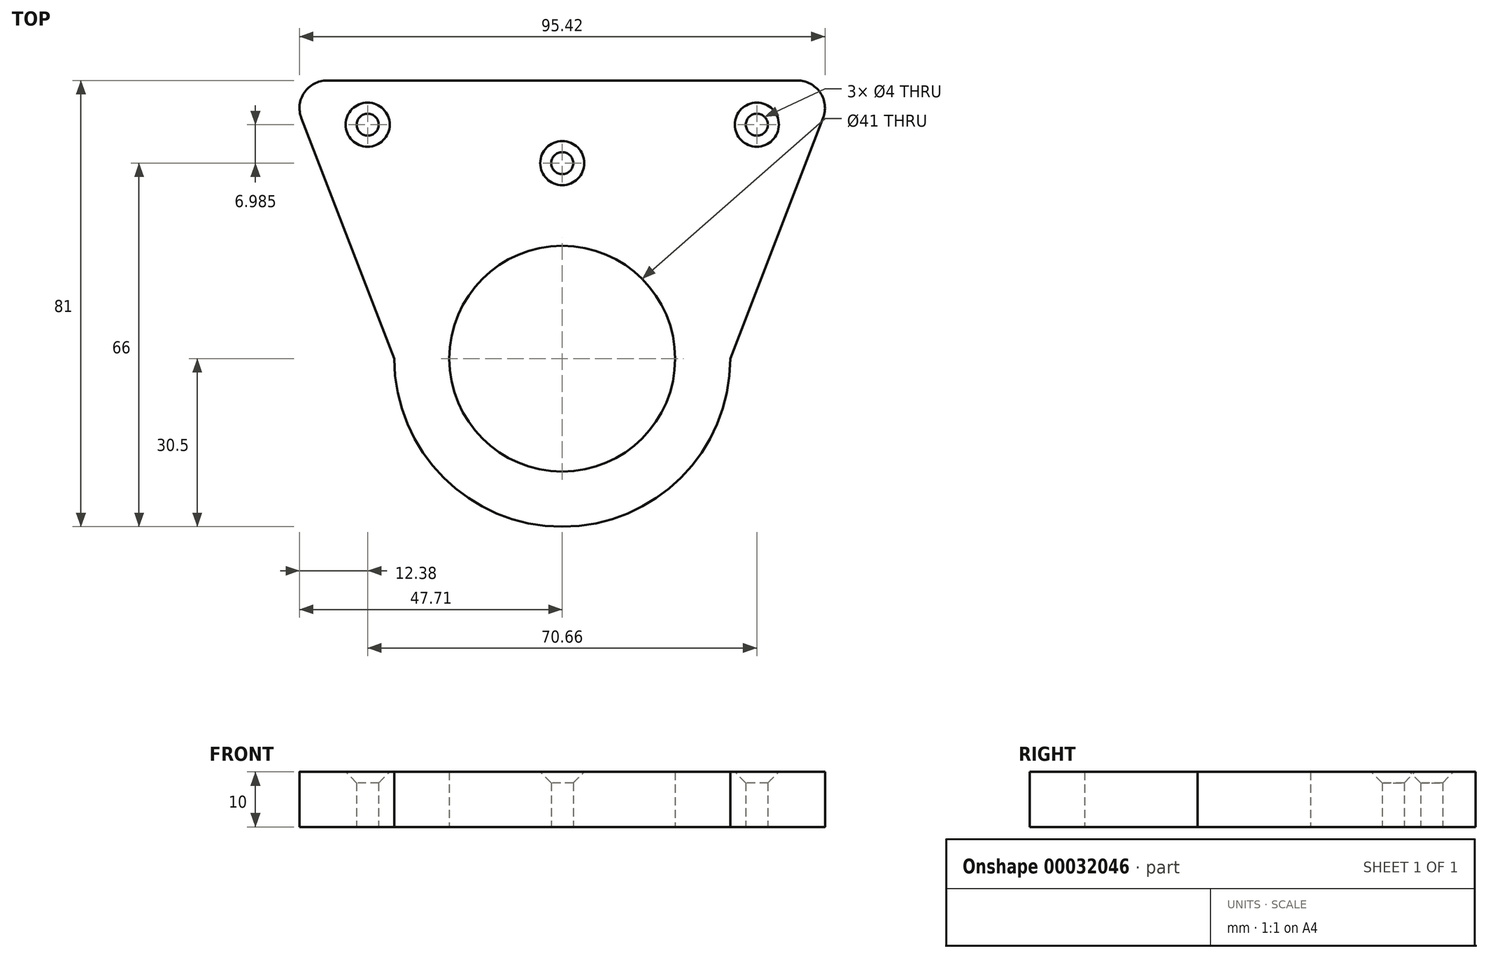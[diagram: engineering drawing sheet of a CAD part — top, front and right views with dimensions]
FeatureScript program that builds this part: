
annotation { "Feature Type Name" : "Feature", "Feature Type Description" : "" }
export const myFeature = defineFeature(function(context is Context, id is Id, definition is map)
    precondition{}
    {
        {
            var Q0;
            Q0=qCreatedBy(makeId("Top.planeOp"),FACE);
            var sketch = newSketch(context, id + "F0", { "sketchPlane" : qUnion([Q0])});
            skCircle(sketch, "E0", {"center": v(0, 0) * mm, "radius": 20.5 * mm});
            skLineSegment(sketch, "E1", {"start": v(0, -20.5) * mm, "end": v(0, -30.5) * mm, "construction": true});
            skLineSegment(sketch, "E2", {"start": v(0, 20.5) * mm, "end": v(0, 50.5) * mm, "construction": true});
            skLineSegment(sketch, "E3", {"start": v(-20.5, 0) * mm, "end": v(-30.5, 0) * mm, "construction": true});
            skLineSegment(sketch, "E4", {"start": v(20.5, 0) * mm, "end": v(30.5, 0) * mm, "construction": true});
            skArc(sketch, "E5", {"start": v(-30.5, 0) * mm, "mid": v(0, -30.5) * mm, "end": v(30.5, 0) * mm});
            skLineSegment(sketch, "E6", {"start": v(50, 50.5) * mm, "end": v(-50, 50.5) * mm});
            skLineSegment(sketch, "E7", {"start": v(-50, 50.5) * mm, "end": v(-30.5, 0) * mm});
            skLineSegment(sketch, "E8", {"start": v(50, 50.5) * mm, "end": v(30.5, 0) * mm});
            skCircle(sketch, "E9", {"center": v(0, 35.5) * mm, "radius": 2 * mm});
            skCircle(sketch, "E10", {"center": v(-35.33, 42.48) * mm, "radius": 2 * mm});
            skCircle(sketch, "E11.MirrorC", {"center": v(35.33, 42.48) * mm, "radius": 2 * mm});
            skSolve(sketch);
        }
        {
            var Q0;
            Q0 = qSketchRegion(id + "F0", true);
            extrude(context, id + "F1", {"entities" : qUnion([Q0]), "depth" : 10 * mm});
        }
        {
            var Q0;
            Q0=makeQuery(id+"F1.opExtrude","CAP_EDGE",EDGE,{"disambiguationData":[OSD([sQuery(id+"F0.wireOp",EDGE,"E10")])],"isStart":false});
            var Q1;
            Q1=makeQuery(id+"F1.opExtrude","CAP_EDGE",EDGE,{"disambiguationData":[OSD([sQuery(id+"F0.wireOp",EDGE,"E9")])],"isStart":false});
            var Q2;
            Q2=makeQuery(id+"F1.opExtrude","CAP_EDGE",EDGE,{"disambiguationData":[OSD([sQuery(id+"F0.wireOp",EDGE,"E11.MirrorC")])],"isStart":false});
            chamfer(context, id + "F2", {"entities" : qUnion([Q0, Q1, Q2]), "width" : 2 * mm, "tangentPropagation" : true});
        }
        {
            var Q0;
            Q0=makeQuery(id+"F1.opExtrude","SWEPT_EDGE",EDGE,{"disambiguationData":[OSD([sQuery(id+"F0.wireOp",EDGE,"E6"),sQuery(id+"F0.wireOp",EDGE,"E8")])]});
            var Q1;
            Q1=makeQuery(id+"F1.opExtrude","SWEPT_EDGE",EDGE,{"disambiguationData":[OSD([sQuery(id+"F0.wireOp",EDGE,"E6"),sQuery(id+"F0.wireOp",EDGE,"E7")])]});
            fillet(context, id + "F3", {"entities" : qUnion([Q0, Q1]), "radius" : 5 * mm, "tangentPropagation" : true, "allowEdgeOverflow" : false});
        }
    });
